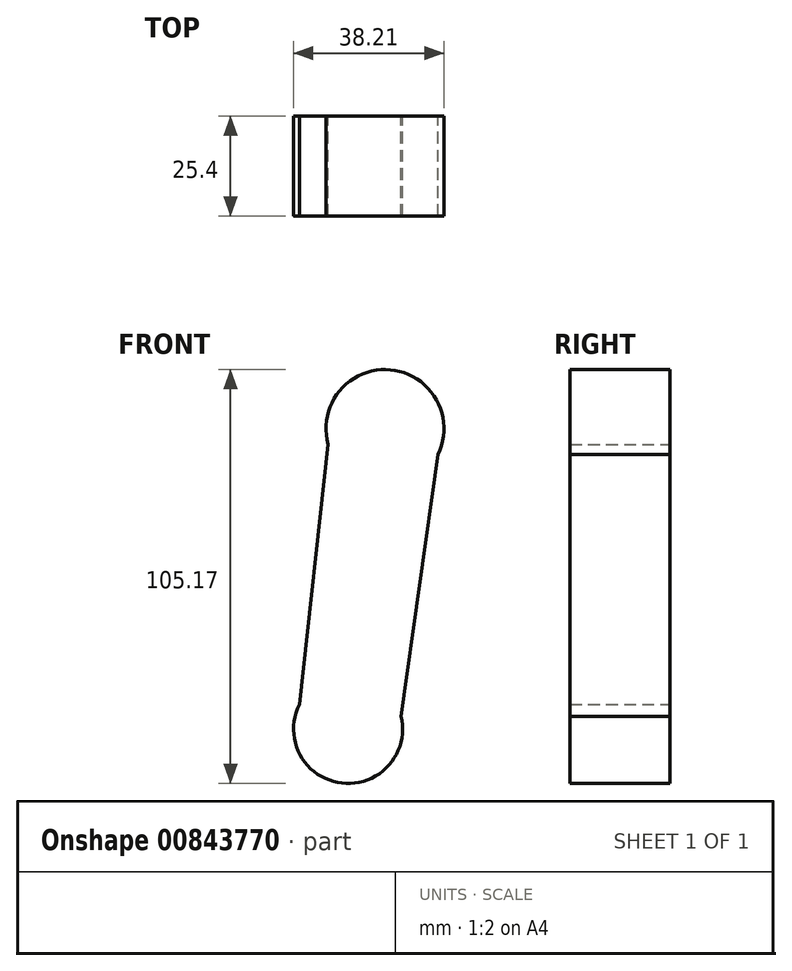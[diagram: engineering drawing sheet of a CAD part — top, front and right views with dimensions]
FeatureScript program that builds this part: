
annotation { "Feature Type Name" : "Feature", "Feature Type Description" : "" }
export const myFeature = defineFeature(function(context is Context, id is Id, definition is map)
    precondition{}
    {
        {
            var Q0;
            Q0=qCreatedBy(makeId("Front.planeOp"),FACE);
            var sketch = newSketch(context, id + "F0", { "sketchPlane" : qUnion([Q0])});
            skCircle(sketch, "E0", {"center": v(-45.54, 43.55) * mm, "radius": 14.98 * mm});
            skCircle(sketch, "E1", {"center": v(-54.9, -32.77) * mm, "radius": 13.86 * mm});
            skLineSegment(sketch, "E2", {"start": v(-59.96, 39.5) * mm, "end": v(-67.3, -26.57) * mm});
            skLineSegment(sketch, "E3", {"start": v(-32.1, 36.93) * mm, "end": v(-41.42, -29.54) * mm});
            skSolve(sketch);
        }
        {
            var Q0;
            {var subQ0=sQuery(id+"F0.wireOp",EDGE,"E0");var subQ1=makeQuery(id+"F0.imprint","INTERSECT",VERTEX,{"derivedFrom":[subQ0,sQuery(id+"F0.wireOp",EDGE,"E2")]});Q0=makeQuery(id+"F0.imprint","IMPRINT",FACE,{"disambiguationData":[TD([[makeQuery(id+"F0.imprint","IMPRINT",EDGE,{"disambiguationData":[TD([[subQ1,-1.0]])],"derivedFrom":subQ0}),1.0]])]});}
            var Q1;
            {var subQ0=sQuery(id+"F0.wireOp",EDGE,"E2");Q1=makeQuery(id+"F0.imprint","IMPRINT",FACE,{"disambiguationData":[TD([[makeQuery(id+"F0.imprint","IMPRINT",EDGE,{"derivedFrom":subQ0}),1.0]])]});}
            var Q2;
            {var subQ0=sQuery(id+"F0.wireOp",EDGE,"E1");var subQ1=makeQuery(id+"F0.imprint","INTERSECT",VERTEX,{"derivedFrom":[subQ0,sQuery(id+"F0.wireOp",EDGE,"E2")]});Q2=makeQuery(id+"F0.imprint","IMPRINT",FACE,{"disambiguationData":[TD([[makeQuery(id+"F0.imprint","IMPRINT",EDGE,{"disambiguationData":[TD([[subQ1,1.0]])],"derivedFrom":subQ0}),1.0]])]});}
            extrude(context, id + "F1", {"entities" : qUnion([Q0, Q1, Q2]), "depth" : 25.4 * mm, "offsetDistance" : 25.4 * mm});
        }
    });
